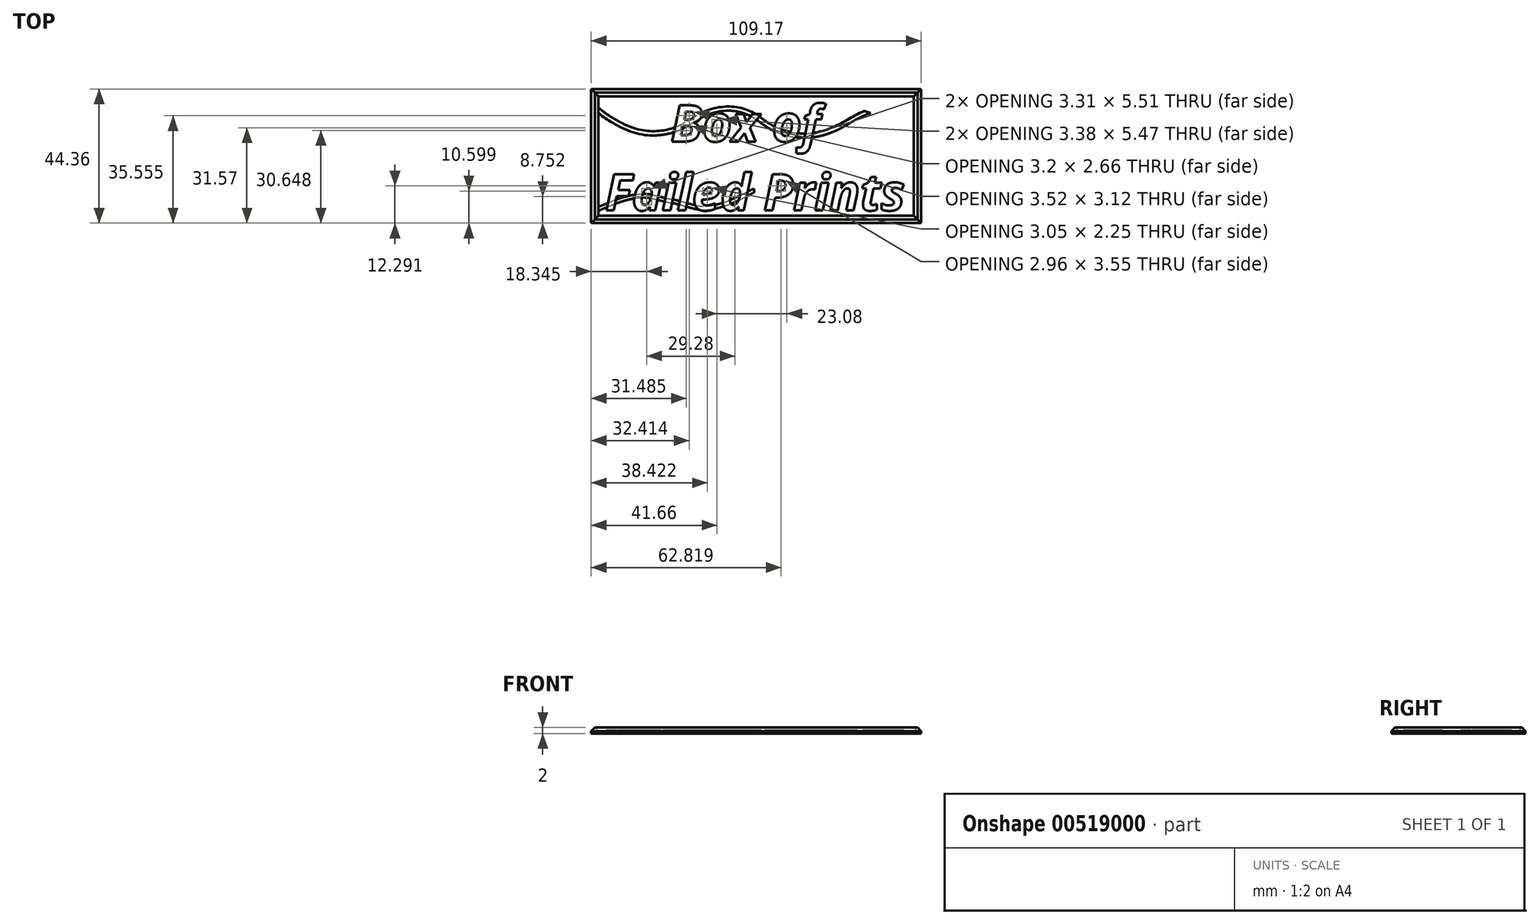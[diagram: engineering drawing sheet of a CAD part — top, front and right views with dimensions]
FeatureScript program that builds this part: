
annotation { "Feature Type Name" : "Feature", "Feature Type Description" : "" }
export const myFeature = defineFeature(function(context is Context, id is Id, definition is map)
    precondition{}
    {
        {
            var Q0;
            Q0=qCreatedBy(makeId("Top.planeOp"),FACE);
            var sketch = newSketch(context, id + "F0", { "sketchPlane" : qUnion([Q0])});
            skText(sketch, "E0", { "text": "     Box of\nFailed Prints", "fontName": "OpenSans-BoldItalic.ttf"});
            skPoint(sketch, "E1", {"position": v(22.9, -6.3) * mm});
            skPoint(sketch, "E2", {"position": v(16.26, 3.29) * mm});
            skPoint(sketch, "E3", {"position": v(-27.04, 4.89) * mm});
            skPoint(sketch, "E4", {"position": v(-27.69, -6.3) * mm});
            skPoint(sketch, "E5", {"position": v(-42.06, -6.3) * mm});
            skPoint(sketch, "E6", {"position": v(38.07, -7.94) * mm});
            skPoint(sketch, "E7", {"position": v(3.67, -16.5) * mm});
            skPoint(sketch, "E8", {"position": v(-5.3, -16.52) * mm});
            skPoint(sketch, "E9", {"position": v(-5.3, 13.1) * mm});
            const initialGuessF0  = {"E0": [-0.0504, 0.00489, 1, 0, 0.01208]};
            skSetInitialGuess(sketch, initialGuessF0);
            skSolve(sketch);
        }
        {
            var Q0;
            Q0=qCreatedBy(makeId("Top.planeOp"),FACE);
            var sketch = newSketch(context, id + "F1", { "sketchPlane" : qUnion([Q0])});
            skLineSegment(sketch, "E10.bottom", {"start": v(-53.75, 21.06) * mm, "end": v(53.02, 21.06) * mm});
            skLineSegment(sketch, "E10.top", {"start": v(-53.75, -20.9) * mm, "end": v(53.02, -20.9) * mm});
            skLineSegment(sketch, "E10.left", {"start": v(-53.75, 21.06) * mm, "end": v(-53.75, -20.9) * mm});
            skLineSegment(sketch, "E10.right", {"start": v(53.02, 21.06) * mm, "end": v(53.02, -20.9) * mm});
            skLineSegment(sketch, "E11.1", {"start": v(-52.57, 19.86) * mm, "end": v(51.82, 19.86) * mm});
            skLineSegment(sketch, "E11.3", {"start": v(-52.55, -19.72) * mm, "end": v(51.83, -19.66) * mm});
            skPoint(sketch, "E12.3", {"position": v(-5.3, -16.52) * mm});
            skPoint(sketch, "E12.4", {"position": v(-27.69, -6.3) * mm});
            skPoint(sketch, "E12.5", {"position": v(-42.06, -6.3) * mm});
            skPoint(sketch, "E12.6", {"position": v(3.67, -16.5) * mm});
            skPoint(sketch, "E12.7", {"position": v(22.9, -6.3) * mm});
            skPoint(sketch, "E12.8", {"position": v(38.07, -7.94) * mm});
            skPoint(sketch, "E13.3.internal.snap0", {"position": v(-0.45, -13.25) * mm});
            skLineSegment(sketch, "E14.0", {"start": v(-54.95, 22.26) * mm, "end": v(54.22, 22.26) * mm});
            skLineSegment(sketch, "E14.1", {"start": v(-54.95, 22.26) * mm, "end": v(-54.95, -22.1) * mm});
            skLineSegment(sketch, "E14.2", {"start": v(-54.95, -22.1) * mm, "end": v(54.22, -22.1) * mm});
            skLineSegment(sketch, "E14.3", {"start": v(54.22, 22.26) * mm, "end": v(54.22, -22.1) * mm});
            skFitSpline(sketch, "E15", {"points": [v(-52.55, -16.74) * mm, v(-45.87, -14.06) * mm, v(-37.44, -12.43) * mm, v(-31.84, -13.48) * mm, v(-24.84, -15) * mm, v(-18.3, -16.51) * mm, v(-9.66, -14.76) * mm, v(-1.84, -11.02) * mm, v(3.76, -8.8) * mm, v(9.6, -8.37) * mm, v(13.33, -9.5) * mm, v(17.65, -13.24) * mm, v(26.29, -14.64) * mm, v(35.04, -13.48) * mm, v(43.68, -9.97) * mm, v(51.82, -6.94) * mm], "startDerivative": vector(94.52, 42) * mm, "endDerivative": vector(110.86, 38.48) * mm});
            skFitSpline(sketch, "E16.0", {"points": [v(-52.07, -17.84) * mm, v(-51.08, -17.4) * mm, v(-49.62, -16.75) * mm, v(-47.57, -15.93) * mm, v(-45.95, -15.34) * mm, v(-44.2, -14.78) * mm, v(-42.4, -14.29) * mm, v(-40.58, -13.9) * mm, v(-39.13, -13.7) * mm, v(-38.06, -13.63) * mm, v(-37.31, -13.62) * mm, v(-36.6, -13.66) * mm, v(-35.7, -13.78) * mm, v(-34.59, -14) * mm, v(-33.42, -14.31) * mm, v(-32.42, -14.57) * mm, v(-31.36, -14.82) * mm, v(-30, -15.1) * mm, v(-28.3, -15.43) * mm, v(-26.92, -15.72) * mm, v(-25.83, -15.97) * mm, v(-25.05, -16.18) * mm, v(-24.27, -16.4) * mm, v(-23.23, -16.7) * mm, v(-21.92, -17.1) * mm, v(-20.54, -17.44) * mm, v(-19.37, -17.63) * mm, v(-18.45, -17.72) * mm, v(-17.5, -17.74) * mm, v(-16.23, -17.68) * mm, v(-14.6, -17.46) * mm, v(-12.63, -17.02) * mm, v(-10.67, -16.42) * mm, v(-8.11, -15.47) * mm, v(-5.71, -14.35) * mm, v(-3.49, -13.22) * mm, v(-1.92, -12.4) * mm, v(-0.45, -11.66) * mm, v(0.92, -11.02) * mm, v(2.25, -10.48) * mm, v(3.36, -10.13) * mm, v(4.28, -9.92) * mm, v(5.24, -9.74) * mm, v(6.47, -9.59) * mm, v(7.7, -9.53) * mm, v(8.64, -9.53) * mm, v(9.32, -9.55) * mm, v(9.96, -9.6) * mm, v(10.73, -9.7) * mm, v(11.4, -9.85) * mm, v(11.98, -10.09) * mm, v(12.4, -10.31) * mm, v(12.8, -10.6) * mm, v(13.24, -10.99) * mm, v(13.72, -11.46) * mm, v(14.41, -12.16) * mm, v(15.2, -12.95) * mm, v(16.13, -13.7) * mm, v(16.79, -14.14) * mm, v(17.36, -14.45) * mm, v(17.95, -14.73) * mm, v(18.71, -15.03) * mm, v(19.67, -15.3) * mm, v(20.99, -15.58) * mm, v(22.69, -15.78) * mm, v(24.41, -15.85) * mm, v(25.77, -15.85) * mm, v(27.1, -15.83) * mm, v(28.74, -15.76) * mm, v(30.67, -15.6) * mm, v(32.58, -15.31) * mm, v(34.47, -14.9) * mm, v(36.36, -14.34) * mm, v(38.21, -13.65) * mm, v(40.04, -12.89) * mm, v(41.83, -12.1) * mm, v(43.59, -11.31) * mm, v(45.31, -10.59) * mm, v(47.04, -9.92) * mm, v(49.34, -9.07) * mm, v(51.06, -8.47) * mm, v(52.22, -8.07) * mm]});
            skFitSpline(sketch, "E17", {"points": [v(-45.87, -14.06) * mm, v(-42.3, -9.7) * mm, v(-42.06, -6.3) * mm, v(-43.55, -3.6) * mm, v(-47.16, -3.05) * mm], "startDerivative": vector(14.66, 14.42) * mm, "endDerivative": vector(-16.79, -0.25) * mm});
            skFitSpline(sketch, "E18", {"points": [v(-43.62, -13.38) * mm, v(-41.38, -9.83) * mm, v(-41.09, -6.74) * mm, v(-42.06, -4.11) * mm, v(-43.2, -2.89) * mm, v(-45.87, -2.24) * mm, v(-47.16, -3.05) * mm], "startDerivative": vector(12.11, 17.54) * mm, "endDerivative": vector(-8.35, -8.39) * mm});
            skFitSpline(sketch, "E19", {"points": [v(-41.3, -14.06) * mm, v(-38.04, -16.51) * mm, v(-31.84, -17.56) * mm, v(-27.98, -17.21) * mm], "startDerivative": vector(8.92, -8.87) * mm, "endDerivative": vector(11.58, 1.72) * mm});
            skFitSpline(sketch, "E20", {"points": [v(-42.64, -14.37) * mm, v(-39.3, -17.28) * mm, v(-33.53, -18.39) * mm, v(-29.44, -18.04) * mm, v(-27.98, -17.21) * mm], "startDerivative": vector(10.87, -12.4) * mm, "endDerivative": vector(7.58, 5.67) * mm});
            skFitSpline(sketch, "E21", {"points": [v(-33.72, -13) * mm, v(-30.55, -11.87) * mm, v(-27.15, -10.06) * mm, v(-26.04, -8.19) * mm, v(-26.45, -7.15) * mm, v(-27.69, -6.3) * mm, v(-30.62, -6.3) * mm, v(-31.84, -7.08) * mm], "startDerivative": vector(17.57, 6.72) * mm, "endDerivative": vector(-8.56, -7.92) * mm});
            skFitSpline(sketch, "E22", {"points": [v(-31.84, -13.48) * mm, v(-27.69, -11.73) * mm, v(-25.55, -9.58) * mm, v(-25.06, -7.91) * mm, v(-25.83, -6.76) * mm, v(-27.07, -5.92) * mm, v(-28.5, -5.75) * mm, v(-30.22, -5.88) * mm, v(-31.3, -6.3) * mm, v(-31.84, -7.08) * mm], "startDerivative": vector(25.72, 8.64) * mm, "endDerivative": vector(-5.63, -10.85) * mm});
            skFitSpline(sketch, "E23", {"points": [v(-22.57, -15.65) * mm, v(-19.68, -14.06) * mm, v(-18.3, -10.78) * mm, v(-17.12, -8.19) * mm, v(-14.31, -7.08) * mm, v(-12.74, -6.3) * mm, v(-11.92, -4.5) * mm, v(-12.41, -3.05) * mm], "startDerivative": vector(19.95, 7.04) * mm, "endDerivative": vector(-6.86, 12.25) * mm});
            skFitSpline(sketch, "E24", {"points": [v(-20.8, -16.14) * mm, v(-19.27, -15) * mm, v(-17.61, -12.61) * mm, v(-16.87, -9.37) * mm, v(-15.4, -8.19) * mm, v(-12.74, -7.08) * mm, v(-11.52, -5.03) * mm, v(-11.66, -3.7) * mm, v(-12.41, -3.05) * mm], "startDerivative": vector(13, 5.53) * mm, "endDerivative": vector(-10.05, 6.42) * mm});
            skFitSpline(sketch, "E25", {"points": [v(-6.4, -14.66) * mm, v(-2.78, -15.38) * mm, v(-0.67, -14.06) * mm, v(-0.45, -13.25) * mm, v(-0.45, -10.34) * mm, v(-1.11, -8.66) * mm, v(-2.53, -7.08) * mm, v(-4.97, -6.3) * mm, v(-6.6, -6.3) * mm, v(-7.74, -5.66) * mm, v(-7.84, -4.2) * mm], "startDerivative": vector(27.63, -11.22) * mm, "endDerivative": vector(2.22, 19.13) * mm});
            skFitSpline(sketch, "E26", {"points": [v(-4.97, -14.06) * mm, v(-3.47, -14.66) * mm, v(-1.9, -14.06) * mm, v(-1.26, -13.25) * mm, v(-1.06, -11.21) * mm, v(-1.55, -9.3) * mm, v(-3.07, -7.58) * mm, v(-5.3, -7.08) * mm, v(-7.2, -6.77) * mm, v(-8.42, -5.66) * mm, v(-8.47, -4.74) * mm, v(-7.84, -4.2) * mm], "startDerivative": vector(15.88, -9.92) * mm, "endDerivative": vector(11.77, 7.08) * mm});
            skFitSpline(sketch, "E27", {"points": [v(8.18, -9.53) * mm, v(10.24, -12.97) * mm, v(14.53, -15) * mm, v(17.8, -14.66) * mm, v(21.88, -12.97) * mm, v(23.9, -9.5) * mm, v(23.9, -8.19) * mm, v(22.9, -6.3) * mm, v(20.64, -4.74) * mm, v(18.17, -4.74) * mm, v(18.25, -4.74) * mm], "startDerivative": vector(12.47, -29.94) * mm, "endDerivative": vector(7.3, 0.3) * mm});
            skFitSpline(sketch, "E28", {"points": [v(6.77, -9.58) * mm, v(8.84, -13.48) * mm, v(13.33, -15.68) * mm, v(17.34, -15.77) * mm, v(22.38, -13.48) * mm, v(24.54, -9.53) * mm, v(24.34, -7.68) * mm, v(22.9, -5.38) * mm, v(20.71, -4.2) * mm, v(18.25, -4.74) * mm], "startDerivative": vector(12.1, -34.35) * mm, "endDerivative": vector(-26.7, -10.01) * mm});
            skFitSpline(sketch, "E29", {"points": [v(32.32, -14.12) * mm, v(34.85, -12.79) * mm, v(37.2, -10.43) * mm, v(37.5, -8.12) * mm, v(36.37, -6.21) * mm, v(36.71, -4.5) * mm, v(38.13, -3.27) * mm, v(40.83, -3.36) * mm], "startDerivative": vector(16.32, 7.02) * mm, "endDerivative": vector(19.35, -3.3) * mm});
            skFitSpline(sketch, "E30", {"points": [v(36.21, -13.1) * mm, v(38.09, -10.82) * mm, v(38.43, -8.71) * mm, v(38.07, -7.94) * mm, v(36.88, -5.99) * mm, v(37.47, -4.37) * mm, v(38.67, -3.56) * mm, v(40.83, -3.36) * mm], "startDerivative": vector(12.78, 11.25) * mm, "endDerivative": vector(13.8, 2.6) * mm});
            skFitSpline(sketch, "E31.trimOffspring", {"points": [v(-52.07, -17.84) * mm, v(-51.08, -17.4) * mm, v(-49.62, -16.75) * mm, v(-47.57, -15.93) * mm, v(-45.95, -15.34) * mm, v(-44.2, -14.78) * mm, v(-42.4, -14.29) * mm, v(-40.58, -13.9) * mm, v(-39.13, -13.7) * mm, v(-38.06, -13.63) * mm, v(-37.31, -13.62) * mm, v(-36.6, -13.66) * mm, v(-35.7, -13.78) * mm, v(-34.59, -14) * mm, v(-33.42, -14.31) * mm, v(-32.42, -14.57) * mm, v(-31.36, -14.82) * mm, v(-30, -15.1) * mm, v(-28.3, -15.43) * mm, v(-26.92, -15.72) * mm, v(-25.83, -15.97) * mm, v(-25.05, -16.18) * mm, v(-24.27, -16.4) * mm, v(-23.23, -16.7) * mm, v(-21.92, -17.1) * mm, v(-20.54, -17.44) * mm, v(-19.37, -17.63) * mm, v(-18.45, -17.72) * mm, v(-17.5, -17.74) * mm, v(-16.23, -17.68) * mm, v(-14.6, -17.46) * mm, v(-12.63, -17.02) * mm, v(-10.67, -16.42) * mm, v(-8.11, -15.47) * mm, v(-5.71, -14.35) * mm, v(-3.49, -13.22) * mm, v(-1.92, -12.4) * mm, v(-0.45, -11.66) * mm, v(0.92, -11.02) * mm, v(2.25, -10.48) * mm, v(3.36, -10.13) * mm, v(4.28, -9.92) * mm, v(5.24, -9.74) * mm, v(6.47, -9.59) * mm, v(7.7, -9.53) * mm, v(8.64, -9.53) * mm, v(9.32, -9.55) * mm, v(9.96, -9.6) * mm, v(10.73, -9.7) * mm, v(11.4, -9.85) * mm, v(11.98, -10.09) * mm, v(12.4, -10.31) * mm, v(12.8, -10.6) * mm, v(13.24, -10.99) * mm, v(13.72, -11.46) * mm, v(14.41, -12.16) * mm, v(15.2, -12.95) * mm, v(16.13, -13.7) * mm, v(16.79, -14.14) * mm, v(17.36, -14.45) * mm, v(17.95, -14.73) * mm, v(18.71, -15.03) * mm, v(19.67, -15.3) * mm, v(20.99, -15.58) * mm, v(22.69, -15.78) * mm, v(24.41, -15.85) * mm, v(25.77, -15.85) * mm, v(27.1, -15.83) * mm, v(28.74, -15.76) * mm, v(30.67, -15.6) * mm, v(32.58, -15.31) * mm, v(34.47, -14.9) * mm, v(36.36, -14.34) * mm, v(38.21, -13.65) * mm, v(40.04, -12.89) * mm, v(41.83, -12.1) * mm, v(43.59, -11.31) * mm, v(45.31, -10.59) * mm, v(47.04, -9.92) * mm, v(49.34, -9.07) * mm, v(51.06, -8.47) * mm, v(52.22, -8.07) * mm]});
            skLineSegment(sketch, "E32", {"start": v(-52.07, -17.84) * mm, "end": v(-52.55, -17.84) * mm});
            skLineSegment(sketch, "E33", {"start": v(-52.55, -17.84) * mm, "end": v(-52.07, -17.84) * mm});
            skFitSpline(sketch, "E34.trimOffspring", {"points": [v(-52.07, -17.84) * mm, v(-51.08, -17.4) * mm, v(-49.62, -16.75) * mm, v(-47.57, -15.93) * mm, v(-45.95, -15.34) * mm, v(-44.2, -14.78) * mm, v(-42.4, -14.29) * mm, v(-40.58, -13.9) * mm, v(-39.13, -13.7) * mm, v(-38.06, -13.63) * mm, v(-37.31, -13.62) * mm, v(-36.6, -13.66) * mm, v(-35.7, -13.78) * mm, v(-34.59, -14) * mm, v(-33.42, -14.31) * mm, v(-32.42, -14.57) * mm, v(-31.36, -14.82) * mm, v(-30, -15.1) * mm, v(-28.3, -15.43) * mm, v(-26.92, -15.72) * mm, v(-25.83, -15.97) * mm, v(-25.05, -16.18) * mm, v(-24.27, -16.4) * mm, v(-23.23, -16.7) * mm, v(-21.92, -17.1) * mm, v(-20.54, -17.44) * mm, v(-19.37, -17.63) * mm, v(-18.45, -17.72) * mm, v(-17.5, -17.74) * mm, v(-16.23, -17.68) * mm, v(-14.6, -17.46) * mm, v(-12.63, -17.02) * mm, v(-10.67, -16.42) * mm, v(-8.11, -15.47) * mm, v(-5.71, -14.35) * mm, v(-3.49, -13.22) * mm, v(-1.92, -12.4) * mm, v(-0.45, -11.66) * mm, v(0.92, -11.02) * mm, v(2.25, -10.48) * mm, v(3.36, -10.13) * mm, v(4.28, -9.92) * mm, v(5.24, -9.74) * mm, v(6.47, -9.59) * mm, v(7.7, -9.53) * mm, v(8.64, -9.53) * mm, v(9.32, -9.55) * mm, v(9.96, -9.6) * mm, v(10.73, -9.7) * mm, v(11.4, -9.85) * mm, v(11.98, -10.09) * mm, v(12.4, -10.31) * mm, v(12.8, -10.6) * mm, v(13.24, -10.99) * mm, v(13.72, -11.46) * mm, v(14.41, -12.16) * mm, v(15.2, -12.95) * mm, v(16.13, -13.7) * mm, v(16.79, -14.14) * mm, v(17.36, -14.45) * mm, v(17.95, -14.73) * mm, v(18.71, -15.03) * mm, v(19.67, -15.3) * mm, v(20.99, -15.58) * mm, v(22.69, -15.78) * mm, v(24.41, -15.85) * mm, v(25.77, -15.85) * mm, v(27.1, -15.83) * mm, v(28.74, -15.76) * mm, v(30.67, -15.6) * mm, v(32.58, -15.31) * mm, v(34.47, -14.9) * mm, v(36.36, -14.34) * mm, v(38.21, -13.65) * mm, v(40.04, -12.89) * mm, v(41.83, -12.1) * mm, v(43.59, -11.31) * mm, v(45.31, -10.59) * mm, v(47.04, -9.92) * mm, v(49.34, -9.07) * mm, v(51.06, -8.47) * mm, v(52.22, -8.07) * mm]});
            skFitSpline(sketch, "E35.trimOffspring", {"points": [v(-52.07, -17.84) * mm, v(-51.08, -17.4) * mm, v(-49.62, -16.75) * mm, v(-47.57, -15.93) * mm, v(-45.95, -15.34) * mm, v(-44.2, -14.78) * mm, v(-42.4, -14.29) * mm, v(-40.58, -13.9) * mm, v(-39.13, -13.7) * mm, v(-38.06, -13.63) * mm, v(-37.31, -13.62) * mm, v(-36.6, -13.66) * mm, v(-35.7, -13.78) * mm, v(-34.59, -14) * mm, v(-33.42, -14.31) * mm, v(-32.42, -14.57) * mm, v(-31.36, -14.82) * mm, v(-30, -15.1) * mm, v(-28.3, -15.43) * mm, v(-26.92, -15.72) * mm, v(-25.83, -15.97) * mm, v(-25.05, -16.18) * mm, v(-24.27, -16.4) * mm, v(-23.23, -16.7) * mm, v(-21.92, -17.1) * mm, v(-20.54, -17.44) * mm, v(-19.37, -17.63) * mm, v(-18.45, -17.72) * mm, v(-17.5, -17.74) * mm, v(-16.23, -17.68) * mm, v(-14.6, -17.46) * mm, v(-12.63, -17.02) * mm, v(-10.67, -16.42) * mm, v(-8.11, -15.47) * mm, v(-5.71, -14.35) * mm, v(-3.49, -13.22) * mm, v(-1.92, -12.4) * mm, v(-0.45, -11.66) * mm, v(0.92, -11.02) * mm, v(2.25, -10.48) * mm, v(3.36, -10.13) * mm, v(4.28, -9.92) * mm, v(5.24, -9.74) * mm, v(6.47, -9.59) * mm, v(7.7, -9.53) * mm, v(8.64, -9.53) * mm, v(9.32, -9.55) * mm, v(9.96, -9.6) * mm, v(10.73, -9.7) * mm, v(11.4, -9.85) * mm, v(11.98, -10.09) * mm, v(12.4, -10.31) * mm, v(12.8, -10.6) * mm, v(13.24, -10.99) * mm, v(13.72, -11.46) * mm, v(14.41, -12.16) * mm, v(15.2, -12.95) * mm, v(16.13, -13.7) * mm, v(16.79, -14.14) * mm, v(17.36, -14.45) * mm, v(17.95, -14.73) * mm, v(18.71, -15.03) * mm, v(19.67, -15.3) * mm, v(20.99, -15.58) * mm, v(22.69, -15.78) * mm, v(24.41, -15.85) * mm, v(25.77, -15.85) * mm, v(27.1, -15.83) * mm, v(28.74, -15.76) * mm, v(30.67, -15.6) * mm, v(32.58, -15.31) * mm, v(34.47, -14.9) * mm, v(36.36, -14.34) * mm, v(38.21, -13.65) * mm, v(40.04, -12.89) * mm, v(41.83, -12.1) * mm, v(43.59, -11.31) * mm, v(45.31, -10.59) * mm, v(47.04, -9.92) * mm, v(49.34, -9.07) * mm, v(51.06, -8.47) * mm, v(52.22, -8.07) * mm]});
            skLineSegment(sketch, "E36", {"start": v(-4.97, -14.06) * mm, "end": v(-5.07, -14.02) * mm});
            skFitSpline(sketch, "E37.trimOffspring", {"points": [v(-52.07, -17.84) * mm, v(-51.08, -17.4) * mm, v(-49.62, -16.75) * mm, v(-47.57, -15.93) * mm, v(-45.95, -15.34) * mm, v(-44.2, -14.78) * mm, v(-42.4, -14.29) * mm, v(-40.58, -13.9) * mm, v(-39.13, -13.7) * mm, v(-38.06, -13.63) * mm, v(-37.31, -13.62) * mm, v(-36.6, -13.66) * mm, v(-35.7, -13.78) * mm, v(-34.59, -14) * mm, v(-33.42, -14.31) * mm, v(-32.42, -14.57) * mm, v(-31.36, -14.82) * mm, v(-30, -15.1) * mm, v(-28.3, -15.43) * mm, v(-26.92, -15.72) * mm, v(-25.83, -15.97) * mm, v(-25.05, -16.18) * mm, v(-24.27, -16.4) * mm, v(-23.23, -16.7) * mm, v(-21.92, -17.1) * mm, v(-20.54, -17.44) * mm, v(-19.37, -17.63) * mm, v(-18.45, -17.72) * mm, v(-17.5, -17.74) * mm, v(-16.23, -17.68) * mm, v(-14.6, -17.46) * mm, v(-12.63, -17.02) * mm, v(-10.67, -16.42) * mm, v(-8.11, -15.47) * mm, v(-5.71, -14.35) * mm, v(-3.49, -13.22) * mm, v(-1.92, -12.4) * mm, v(-0.45, -11.66) * mm, v(0.92, -11.02) * mm, v(2.25, -10.48) * mm, v(3.36, -10.13) * mm, v(4.28, -9.92) * mm, v(5.24, -9.74) * mm, v(6.47, -9.59) * mm, v(7.7, -9.53) * mm, v(8.64, -9.53) * mm, v(9.32, -9.55) * mm, v(9.96, -9.6) * mm, v(10.73, -9.7) * mm, v(11.4, -9.85) * mm, v(11.98, -10.09) * mm, v(12.4, -10.31) * mm, v(12.8, -10.6) * mm, v(13.24, -10.99) * mm, v(13.72, -11.46) * mm, v(14.41, -12.16) * mm, v(15.2, -12.95) * mm, v(16.13, -13.7) * mm, v(16.79, -14.14) * mm, v(17.36, -14.45) * mm, v(17.95, -14.73) * mm, v(18.71, -15.03) * mm, v(19.67, -15.3) * mm, v(20.99, -15.58) * mm, v(22.69, -15.78) * mm, v(24.41, -15.85) * mm, v(25.77, -15.85) * mm, v(27.1, -15.83) * mm, v(28.74, -15.76) * mm, v(30.67, -15.6) * mm, v(32.58, -15.31) * mm, v(34.47, -14.9) * mm, v(36.36, -14.34) * mm, v(38.21, -13.65) * mm, v(40.04, -12.89) * mm, v(41.83, -12.1) * mm, v(43.59, -11.31) * mm, v(45.31, -10.59) * mm, v(47.04, -9.92) * mm, v(49.34, -9.07) * mm, v(51.06, -8.47) * mm, v(52.22, -8.07) * mm]});
            skFitSpline(sketch, "E38.trimOffspring", {"points": [v(-52.07, -17.84) * mm, v(-51.08, -17.4) * mm, v(-49.62, -16.75) * mm, v(-47.57, -15.93) * mm, v(-45.95, -15.34) * mm, v(-44.2, -14.78) * mm, v(-42.4, -14.29) * mm, v(-40.58, -13.9) * mm, v(-39.13, -13.7) * mm, v(-38.06, -13.63) * mm, v(-37.31, -13.62) * mm, v(-36.6, -13.66) * mm, v(-35.7, -13.78) * mm, v(-34.59, -14) * mm, v(-33.42, -14.31) * mm, v(-32.42, -14.57) * mm, v(-31.36, -14.82) * mm, v(-30, -15.1) * mm, v(-28.3, -15.43) * mm, v(-26.92, -15.72) * mm, v(-25.83, -15.97) * mm, v(-25.05, -16.18) * mm, v(-24.27, -16.4) * mm, v(-23.23, -16.7) * mm, v(-21.92, -17.1) * mm, v(-20.54, -17.44) * mm, v(-19.37, -17.63) * mm, v(-18.45, -17.72) * mm, v(-17.5, -17.74) * mm, v(-16.23, -17.68) * mm, v(-14.6, -17.46) * mm, v(-12.63, -17.02) * mm, v(-10.67, -16.42) * mm, v(-8.11, -15.47) * mm, v(-5.71, -14.35) * mm, v(-3.49, -13.22) * mm, v(-1.92, -12.4) * mm, v(-0.45, -11.66) * mm, v(0.92, -11.02) * mm, v(2.25, -10.48) * mm, v(3.36, -10.13) * mm, v(4.28, -9.92) * mm, v(5.24, -9.74) * mm, v(6.47, -9.59) * mm, v(7.7, -9.53) * mm, v(8.64, -9.53) * mm, v(9.32, -9.55) * mm, v(9.96, -9.6) * mm, v(10.73, -9.7) * mm, v(11.4, -9.85) * mm, v(11.98, -10.09) * mm, v(12.4, -10.31) * mm, v(12.8, -10.6) * mm, v(13.24, -10.99) * mm, v(13.72, -11.46) * mm, v(14.41, -12.16) * mm, v(15.2, -12.95) * mm, v(16.13, -13.7) * mm, v(16.79, -14.14) * mm, v(17.36, -14.45) * mm, v(17.95, -14.73) * mm, v(18.71, -15.03) * mm, v(19.67, -15.3) * mm, v(20.99, -15.58) * mm, v(22.69, -15.78) * mm, v(24.41, -15.85) * mm, v(25.77, -15.85) * mm, v(27.1, -15.83) * mm, v(28.74, -15.76) * mm, v(30.67, -15.6) * mm, v(32.58, -15.31) * mm, v(34.47, -14.9) * mm, v(36.36, -14.34) * mm, v(38.21, -13.65) * mm, v(40.04, -12.89) * mm, v(41.83, -12.1) * mm, v(43.59, -11.31) * mm, v(45.31, -10.59) * mm, v(47.04, -9.92) * mm, v(49.34, -9.07) * mm, v(51.06, -8.47) * mm, v(52.22, -8.07) * mm]});
            skPoint(sketch, "E39.end.orphan", {"position": v(5.4, -8.37) * mm});
            skLineSegment(sketch, "E40.trimOffspring", {"start": v(51.82, -8.2) * mm, "end": v(51.83, -19.66) * mm});
            skLineSegment(sketch, "E41", {"start": v(-52.57, 19.86) * mm, "end": v(-52.55, -19.72) * mm});
            skLineSegment(sketch, "E42", {"start": v(-52.57, 19.86) * mm, "end": v(-54.95, 22.26) * mm});
            skLineSegment(sketch, "E43", {"start": v(-52.55, -19.72) * mm, "end": v(-54.95, -22.1) * mm});
            skLineSegment(sketch, "E44", {"start": v(-52.55, -16.74) * mm, "end": v(-47.44, -14.6) * mm});
            skLineSegment(sketch, "E45.trimOffspring", {"start": v(51.82, -6.94) * mm, "end": v(51.83, -19.66) * mm});
            skLineSegment(sketch, "E46", {"start": v(51.82, 19.86) * mm, "end": v(51.82, -6.94) * mm});
            skFitSpline(sketch, "E47", {"points": [v(-52.57, 16.08) * mm, v(-49.1, 13.5) * mm, v(-40.35, 9.2) * mm, v(-31.83, 8.5) * mm, v(-25.06, 10.6) * mm, v(-17, 15.03) * mm, v(-6.97, 16.31) * mm, v(0, 13.63) * mm, v(4.82, 10.36) * mm, v(14.4, 7.56) * mm, v(25.13, 9.66) * mm, v(33.42, 14.1) * mm, v(43, 16.66) * mm, v(50.11, 14.91) * mm, v(51.82, 13.5) * mm], "startDerivative": vector(55.97, -44.86) * mm, "endDerivative": vector(34.72, -36.64) * mm});
            skFitSpline(sketch, "E48.0", {"points": [v(-53.44, 14.99) * mm, v(-53.15, 14.75) * mm, v(-52.56, 14.28) * mm, v(-51.58, 13.52) * mm, v(-50.63, 12.85) * mm, v(-49.76, 12.26) * mm, v(-48.8, 11.65) * mm, v(-47.47, 10.85) * mm, v(-45.7, 9.88) * mm, v(-43.8, 8.97) * mm, v(-41.82, 8.17) * mm, v(-39.81, 7.55) * mm, v(-37.84, 7.15) * mm, v(-35.9, 6.94) * mm, v(-34.03, 6.9) * mm, v(-32.22, 7.02) * mm, v(-30.48, 7.25) * mm, v(-28.8, 7.62) * mm, v(-27.15, 8.13) * mm, v(-25.8, 8.67) * mm, v(-24.72, 9.18) * mm, v(-23.65, 9.75) * mm, v(-22.35, 10.52) * mm, v(-20.79, 11.48) * mm, v(-19.21, 12.41) * mm, v(-17.6, 13.27) * mm, v(-15.94, 13.97) * mm, v(-14.16, 14.51) * mm, v(-12.32, 14.89) * mm, v(-10.48, 15.08) * mm, v(-8.97, 15.1) * mm, v(-7.81, 15.01) * mm, v(-6.7, 14.87) * mm, v(-5.35, 14.57) * mm, v(-3.85, 14.07) * mm, v(-2.45, 13.44) * mm, v(-1.17, 12.73) * mm, v(-0.02, 11.97) * mm, v(1.09, 11.16) * mm, v(2.27, 10.3) * mm, v(3.61, 9.41) * mm, v(5.2, 8.55) * mm, v(6.98, 7.77) * mm, v(8.94, 7.1) * mm, v(11.02, 6.57) * mm, v(13.2, 6.21) * mm, v(15.42, 6.09) * mm, v(17.63, 6.2) * mm, v(19.8, 6.51) * mm, v(21.9, 7) * mm, v(23.93, 7.64) * mm, v(25.85, 8.42) * mm, v(27.63, 9.29) * mm, v(29.3, 10.2) * mm, v(30.9, 11.13) * mm, v(32.5, 12.04) * mm, v(34.1, 12.89) * mm, v(35.77, 13.66) * mm, v(37.5, 14.31) * mm, v(39.27, 14.83) * mm, v(40.74, 15.11) * mm, v(41.9, 15.23) * mm, v(42.77, 15.27) * mm, v(43.63, 15.25) * mm, v(44.78, 15.15) * mm, v(46.18, 14.9) * mm, v(47.44, 14.54) * mm, v(48.32, 14.22) * mm, v(48.9, 13.97) * mm, v(49.38, 13.72) * mm, v(49.75, 13.5) * mm, v(50.05, 13.27) * mm, v(50.39, 12.98) * mm, v(50.62, 12.74) * mm, v(50.8, 12.55) * mm]});
            skLineSegment(sketch, "E49", {"start": v(50.8, 12.55) * mm, "end": v(51.82, 11.45) * mm});
            skFitSpline(sketch, "E50", {"points": [v(-46.15, 11.73) * mm, v(-38.67, 12.15) * mm, v(-36.08, 14.24) * mm, v(-36.94, 15.97) * mm, v(-39.65, 16.46) * mm, v(-40.51, 15.35) * mm], "startDerivative": vector(26.26, -1.25) * mm, "endDerivative": vector(-4.24, -10.15) * mm});
            skFitSpline(sketch, "E51", {"points": [v(-44.2, 10.72) * mm, v(-39.99, 10.87) * mm, v(-36.44, 12.33) * mm, v(-35.34, 14.3) * mm, v(-35.78, 15.63) * mm, v(-36.92, 16.54) * mm, v(-38.49, 17.02) * mm, v(-39.88, 16.94) * mm, v(-40.46, 16.21) * mm, v(-40.51, 15.35) * mm], "startDerivative": vector(25.11, -0.87) * mm, "endDerivative": vector(0.73, -11.43) * mm});
            skFitSpline(sketch, "E52.trimOffspring", {"points": [v(-52.57, 16.08) * mm, v(-49.1, 13.5) * mm, v(-40.35, 9.2) * mm, v(-31.83, 8.5) * mm, v(-25.06, 10.6) * mm, v(-17, 15.03) * mm, v(-6.97, 16.31) * mm, v(0, 13.63) * mm, v(4.82, 10.36) * mm, v(14.4, 7.56) * mm, v(25.13, 9.66) * mm, v(33.42, 14.1) * mm, v(43, 16.66) * mm, v(50.11, 14.91) * mm, v(51.82, 13.5) * mm], "startDerivative": vector(55.97, -44.86) * mm, "endDerivative": vector(34.72, -36.64) * mm});
            skFitSpline(sketch, "E53", {"points": [v(-33.26, 6.96) * mm, v(-31.83, 5.05) * mm, v(-28.54, 3.22) * mm, v(-24.48, 3.52) * mm, v(-23.01, 4.8) * mm, v(-21.59, 6.11) * mm, v(-19.83, 6.33) * mm, v(-18.26, 5.57) * mm, v(-17.93, 5.05) * mm], "startDerivative": vector(9.14, -14.66) * mm, "endDerivative": vector(3.25, -7.53) * mm});
            skFitSpline(sketch, "E54", {"points": [v(-34.54, 6.93) * mm, v(-32.97, 5.2) * mm, v(-30.92, 3.52) * mm, v(-28.43, 2.53) * mm, v(-25.83, 2.57) * mm, v(-24.08, 3.11) * mm, v(-22.76, 4.52) * mm, v(-21.67, 5.66) * mm, v(-20.51, 6.15) * mm, v(-19.33, 5.94) * mm, v(-18.53, 5.57) * mm, v(-17.93, 5.05) * mm], "startDerivative": vector(14.25, -16.4) * mm, "endDerivative": vector(9.39, -8.93) * mm});
            skFitSpline(sketch, "E55.trimOffspring", {"points": [v(-53.44, 14.99) * mm, v(-53.15, 14.75) * mm, v(-52.56, 14.28) * mm, v(-51.58, 13.52) * mm, v(-50.63, 12.85) * mm, v(-49.76, 12.26) * mm, v(-48.8, 11.65) * mm, v(-47.47, 10.85) * mm, v(-45.7, 9.88) * mm, v(-43.8, 8.97) * mm, v(-41.82, 8.17) * mm, v(-39.81, 7.55) * mm, v(-37.84, 7.15) * mm, v(-35.9, 6.94) * mm, v(-34.03, 6.9) * mm, v(-32.22, 7.02) * mm, v(-30.48, 7.25) * mm, v(-28.8, 7.62) * mm, v(-27.15, 8.13) * mm, v(-25.8, 8.67) * mm, v(-24.72, 9.18) * mm, v(-23.65, 9.75) * mm, v(-22.35, 10.52) * mm, v(-20.79, 11.48) * mm, v(-19.21, 12.41) * mm, v(-17.6, 13.27) * mm, v(-15.94, 13.97) * mm, v(-14.16, 14.51) * mm, v(-12.32, 14.89) * mm, v(-10.48, 15.08) * mm, v(-8.97, 15.1) * mm, v(-7.81, 15.01) * mm, v(-6.7, 14.87) * mm, v(-5.35, 14.57) * mm, v(-3.85, 14.07) * mm, v(-2.45, 13.44) * mm, v(-1.17, 12.73) * mm, v(-0.02, 11.97) * mm, v(1.09, 11.16) * mm, v(2.27, 10.3) * mm, v(3.61, 9.41) * mm, v(5.2, 8.55) * mm, v(6.98, 7.77) * mm, v(8.94, 7.1) * mm, v(11.02, 6.57) * mm, v(13.2, 6.21) * mm, v(15.42, 6.09) * mm, v(17.63, 6.2) * mm, v(19.8, 6.51) * mm, v(21.9, 7) * mm, v(23.93, 7.64) * mm, v(25.85, 8.42) * mm, v(27.63, 9.29) * mm, v(29.3, 10.2) * mm, v(30.9, 11.13) * mm, v(32.5, 12.04) * mm, v(34.1, 12.89) * mm, v(35.77, 13.66) * mm, v(37.5, 14.31) * mm, v(39.27, 14.83) * mm, v(40.74, 15.11) * mm, v(41.9, 15.23) * mm, v(42.77, 15.27) * mm, v(43.63, 15.25) * mm, v(44.78, 15.15) * mm, v(46.18, 14.9) * mm, v(47.44, 14.54) * mm, v(48.32, 14.22) * mm, v(48.9, 13.97) * mm, v(49.38, 13.72) * mm, v(49.75, 13.5) * mm, v(50.05, 13.27) * mm, v(50.39, 12.98) * mm, v(50.62, 12.74) * mm, v(50.8, 12.55) * mm]});
            skFitSpline(sketch, "E56", {"points": [v(-19.85, 12.03) * mm, v(-16.5, 11.65) * mm, v(-11.84, 10.3) * mm, v(-8.94, 8.14) * mm, v(-7.29, 6.48) * mm, v(-5.12, 4.93) * mm, v(-1.5, 5.03) * mm, v(0, 6.48) * mm, v(1.1, 8.55) * mm, v(1.2, 8.45) * mm], "startDerivative": vector(24.63, -1.81) * mm, "endDerivative": vector(3.2, -6.58) * mm});
            skFitSpline(sketch, "E57", {"points": [v(-21.67, 10.94) * mm, v(-15.98, 10.2) * mm, v(-12.05, 9.2) * mm, v(-8.94, 6.69) * mm, v(-6.85, 4.93) * mm, v(-4.5, 4.1) * mm, v(-2.29, 4.15) * mm, v(-0.46, 4.84) * mm, v(0.8, 6.93) * mm, v(1.2, 8.45) * mm], "startDerivative": vector(37.95, -4.74) * mm, "endDerivative": vector(3.47, 17.32) * mm});
            skFitSpline(sketch, "E58.trimOffspring", {"points": [v(-53.44, 14.99) * mm, v(-53.15, 14.75) * mm, v(-52.56, 14.28) * mm, v(-51.58, 13.52) * mm, v(-50.63, 12.85) * mm, v(-49.76, 12.26) * mm, v(-48.8, 11.65) * mm, v(-47.47, 10.85) * mm, v(-45.7, 9.88) * mm, v(-43.8, 8.97) * mm, v(-41.82, 8.17) * mm, v(-39.81, 7.55) * mm, v(-37.84, 7.15) * mm, v(-35.9, 6.94) * mm, v(-34.03, 6.9) * mm, v(-32.22, 7.02) * mm, v(-30.48, 7.25) * mm, v(-28.8, 7.62) * mm, v(-27.15, 8.13) * mm, v(-25.8, 8.67) * mm, v(-24.72, 9.18) * mm, v(-23.65, 9.75) * mm, v(-22.35, 10.52) * mm, v(-20.79, 11.48) * mm, v(-19.21, 12.41) * mm, v(-17.6, 13.27) * mm, v(-15.94, 13.97) * mm, v(-14.16, 14.51) * mm, v(-12.32, 14.89) * mm, v(-10.48, 15.08) * mm, v(-8.97, 15.1) * mm, v(-7.81, 15.01) * mm, v(-6.7, 14.87) * mm, v(-5.35, 14.57) * mm, v(-3.85, 14.07) * mm, v(-2.45, 13.44) * mm, v(-1.17, 12.73) * mm, v(-0.02, 11.97) * mm, v(1.09, 11.16) * mm, v(2.27, 10.3) * mm, v(3.61, 9.41) * mm, v(5.2, 8.55) * mm, v(6.98, 7.77) * mm, v(8.94, 7.1) * mm, v(11.02, 6.57) * mm, v(13.2, 6.21) * mm, v(15.42, 6.09) * mm, v(17.63, 6.2) * mm, v(19.8, 6.51) * mm, v(21.9, 7) * mm, v(23.93, 7.64) * mm, v(25.85, 8.42) * mm, v(27.63, 9.29) * mm, v(29.3, 10.2) * mm, v(30.9, 11.13) * mm, v(32.5, 12.04) * mm, v(34.1, 12.89) * mm, v(35.77, 13.66) * mm, v(37.5, 14.31) * mm, v(39.27, 14.83) * mm, v(40.74, 15.11) * mm, v(41.9, 15.23) * mm, v(42.77, 15.27) * mm, v(43.63, 15.25) * mm, v(44.78, 15.15) * mm, v(46.18, 14.9) * mm, v(47.44, 14.54) * mm, v(48.32, 14.22) * mm, v(48.9, 13.97) * mm, v(49.38, 13.72) * mm, v(49.75, 13.5) * mm, v(50.05, 13.27) * mm, v(50.39, 12.98) * mm, v(50.62, 12.74) * mm, v(50.8, 12.55) * mm]});
            skFitSpline(sketch, "E59", {"points": [v(3.18, 11.39) * mm, v(5.55, 11.02) * mm, v(10.46, 10.94) * mm, v(14.07, 12.37) * mm, v(16.07, 14.68) * mm, v(18.34, 15.37) * mm, v(20.86, 14.8) * mm, v(22.6, 13.63) * mm, v(22.86, 12.41) * mm, v(22.38, 11.2) * mm], "startDerivative": vector(19.51, -3.65) * mm, "endDerivative": vector(-7.72, -14.98) * mm});
            skFitSpline(sketch, "E60", {"points": [v(4.82, 10.36) * mm, v(8.16, 10.02) * mm, v(11.64, 10.36) * mm, v(14.38, 11.8) * mm, v(15.9, 13.8) * mm, v(17.68, 14.76) * mm, v(20.16, 14.59) * mm, v(21.73, 13.8) * mm, v(21.97, 13.63) * mm, v(22.4, 13.22) * mm, v(22.68, 12.7) * mm, v(22.6, 12.08) * mm, v(22.38, 11.2) * mm], "startDerivative": vector(27.39, -3.72) * mm, "endDerivative": vector(-3.54, -14.52) * mm});
            skFitSpline(sketch, "E61.trimOffspring", {"points": [v(-52.57, 16.08) * mm, v(-49.1, 13.5) * mm, v(-40.35, 9.2) * mm, v(-31.83, 8.5) * mm, v(-25.06, 10.6) * mm, v(-17, 15.03) * mm, v(-6.97, 16.31) * mm, v(0, 13.63) * mm, v(4.82, 10.36) * mm, v(14.4, 7.56) * mm, v(25.13, 9.66) * mm, v(33.42, 14.1) * mm, v(43, 16.66) * mm, v(50.11, 14.91) * mm, v(51.82, 13.5) * mm], "startDerivative": vector(55.97, -44.86) * mm, "endDerivative": vector(34.72, -36.64) * mm});
            skFitSpline(sketch, "E62", {"points": [v(12.3, 6.37) * mm, v(14.51, 5.17) * mm, v(16.43, 3.2) * mm, v(17, 1.03) * mm, v(15.7, -0.93) * mm, v(13.53, -1.5) * mm, v(11, -0.99) * mm, v(9.6, 0) * mm, v(9.86, 1.4) * mm, v(11.15, 2.32) * mm, v(11.72, 2.12) * mm], "startDerivative": vector(19.8, -9.39) * mm, "endDerivative": vector(8.93, -6.2) * mm});
            skFitSpline(sketch, "E63", {"points": [v(10.43, 6.73) * mm, v(12.86, 5.17) * mm, v(14.57, 4.08) * mm, v(15.8, 2.63) * mm, v(16.22, 0.67) * mm, v(15.24, -0.52) * mm, v(13.58, -0.93) * mm, v(11, -0.47) * mm, v(10, 0) * mm, v(9.83, 0.7) * mm, v(10.38, 1.61) * mm, v(11, 2.09) * mm, v(11.3, 2.13) * mm, v(11.72, 2.12) * mm], "startDerivative": vector(22.23, -15.04) * mm, "endDerivative": vector(10.22, -0.52) * mm});
            skFitSpline(sketch, "E64.trimOffspring", {"points": [v(-53.44, 14.99) * mm, v(-53.15, 14.75) * mm, v(-52.56, 14.28) * mm, v(-51.58, 13.52) * mm, v(-50.63, 12.85) * mm, v(-49.76, 12.26) * mm, v(-48.8, 11.65) * mm, v(-47.47, 10.85) * mm, v(-45.7, 9.88) * mm, v(-43.8, 8.97) * mm, v(-41.82, 8.17) * mm, v(-39.81, 7.55) * mm, v(-37.84, 7.15) * mm, v(-35.9, 6.94) * mm, v(-34.03, 6.9) * mm, v(-32.22, 7.02) * mm, v(-30.48, 7.25) * mm, v(-28.8, 7.62) * mm, v(-27.15, 8.13) * mm, v(-25.8, 8.67) * mm, v(-24.72, 9.18) * mm, v(-23.65, 9.75) * mm, v(-22.35, 10.52) * mm, v(-20.79, 11.48) * mm, v(-19.21, 12.41) * mm, v(-17.6, 13.27) * mm, v(-15.94, 13.97) * mm, v(-14.16, 14.51) * mm, v(-12.32, 14.89) * mm, v(-10.48, 15.08) * mm, v(-8.97, 15.1) * mm, v(-7.81, 15.01) * mm, v(-6.7, 14.87) * mm, v(-5.35, 14.57) * mm, v(-3.85, 14.07) * mm, v(-2.45, 13.44) * mm, v(-1.17, 12.73) * mm, v(-0.02, 11.97) * mm, v(1.09, 11.16) * mm, v(2.27, 10.3) * mm, v(3.61, 9.41) * mm, v(5.2, 8.55) * mm, v(6.98, 7.77) * mm, v(8.94, 7.1) * mm, v(11.02, 6.57) * mm, v(13.2, 6.21) * mm, v(15.42, 6.09) * mm, v(17.63, 6.2) * mm, v(19.8, 6.51) * mm, v(21.9, 7) * mm, v(23.93, 7.64) * mm, v(25.85, 8.42) * mm, v(27.63, 9.29) * mm, v(29.3, 10.2) * mm, v(30.9, 11.13) * mm, v(32.5, 12.04) * mm, v(34.1, 12.89) * mm, v(35.77, 13.66) * mm, v(37.5, 14.31) * mm, v(39.27, 14.83) * mm, v(40.74, 15.11) * mm, v(41.9, 15.23) * mm, v(42.77, 15.27) * mm, v(43.63, 15.25) * mm, v(44.78, 15.15) * mm, v(46.18, 14.9) * mm, v(47.44, 14.54) * mm, v(48.32, 14.22) * mm, v(48.9, 13.97) * mm, v(49.38, 13.72) * mm, v(49.75, 13.5) * mm, v(50.05, 13.27) * mm, v(50.39, 12.98) * mm, v(50.62, 12.74) * mm, v(50.8, 12.55) * mm]});
            skFitSpline(sketch, "E65", {"points": [v(24.2, 7.77) * mm, v(28, 8.15) * mm, v(31.3, 9.25) * mm, v(34.07, 10.27) * mm, v(36.42, 9.4) * mm, v(38.54, 7.93) * mm, v(41.9, 7.5) * mm, v(43.37, 10.42) * mm, v(42.12, 13.42) * mm, v(40.51, 14.22) * mm, v(35.4, 15.76) * mm, v(32.03, 16.27) * mm, v(30.64, 14.8) * mm, v(30.56, 14.8) * mm], "startDerivative": vector(42.5, 2.08) * mm, "endDerivative": vector(-4.74, 2.48) * mm});
            skFitSpline(sketch, "E66", {"points": [v(28.16, 9.58) * mm, v(31.07, 10.34) * mm, v(34, 11.3) * mm, v(36.42, 10.42) * mm, v(39.27, 8.44) * mm, v(41.24, 8.15) * mm, v(42.49, 9.61) * mm, v(41.98, 12.4) * mm, v(38.83, 13.93) * mm, v(34.55, 15.36) * mm, v(32.9, 16) * mm, v(32.06, 15.76) * mm, v(30.64, 14.8) * mm], "startDerivative": vector(31.77, 6.34) * mm, "endDerivative": vector(-22.1, -15.6) * mm});
            skFitSpline(sketch, "E67.trimOffspring", {"points": [v(-53.44, 14.99) * mm, v(-53.15, 14.75) * mm, v(-52.56, 14.28) * mm, v(-51.58, 13.52) * mm, v(-50.63, 12.85) * mm, v(-49.76, 12.26) * mm, v(-48.8, 11.65) * mm, v(-47.47, 10.85) * mm, v(-45.7, 9.88) * mm, v(-43.8, 8.97) * mm, v(-41.82, 8.17) * mm, v(-39.81, 7.55) * mm, v(-37.84, 7.15) * mm, v(-35.9, 6.94) * mm, v(-34.03, 6.9) * mm, v(-32.22, 7.02) * mm, v(-30.48, 7.25) * mm, v(-28.8, 7.62) * mm, v(-27.15, 8.13) * mm, v(-25.8, 8.67) * mm, v(-24.72, 9.18) * mm, v(-23.65, 9.75) * mm, v(-22.35, 10.52) * mm, v(-20.79, 11.48) * mm, v(-19.21, 12.41) * mm, v(-17.6, 13.27) * mm, v(-15.94, 13.97) * mm, v(-14.16, 14.51) * mm, v(-12.32, 14.89) * mm, v(-10.48, 15.08) * mm, v(-8.97, 15.1) * mm, v(-7.81, 15.01) * mm, v(-6.7, 14.87) * mm, v(-5.35, 14.57) * mm, v(-3.85, 14.07) * mm, v(-2.45, 13.44) * mm, v(-1.17, 12.73) * mm, v(-0.02, 11.97) * mm, v(1.09, 11.16) * mm, v(2.27, 10.3) * mm, v(3.61, 9.41) * mm, v(5.2, 8.55) * mm, v(6.98, 7.77) * mm, v(8.94, 7.1) * mm, v(11.02, 6.57) * mm, v(13.2, 6.21) * mm, v(15.42, 6.09) * mm, v(17.63, 6.2) * mm, v(19.8, 6.51) * mm, v(21.9, 7) * mm, v(23.93, 7.64) * mm, v(25.85, 8.42) * mm, v(27.63, 9.29) * mm, v(29.3, 10.2) * mm, v(30.9, 11.13) * mm, v(32.5, 12.04) * mm, v(34.1, 12.89) * mm, v(35.77, 13.66) * mm, v(37.5, 14.31) * mm, v(39.27, 14.83) * mm, v(40.74, 15.11) * mm, v(41.9, 15.23) * mm, v(42.77, 15.27) * mm, v(43.63, 15.25) * mm, v(44.78, 15.15) * mm, v(46.18, 14.9) * mm, v(47.44, 14.54) * mm, v(48.32, 14.22) * mm, v(48.9, 13.97) * mm, v(49.38, 13.72) * mm, v(49.75, 13.5) * mm, v(50.05, 13.27) * mm, v(50.39, 12.98) * mm, v(50.62, 12.74) * mm, v(50.8, 12.55) * mm]});
            skFitSpline(sketch, "E68.trimOffspring", {"points": [v(-53.44, 14.99) * mm, v(-53.15, 14.75) * mm, v(-52.56, 14.28) * mm, v(-51.58, 13.52) * mm, v(-50.63, 12.85) * mm, v(-49.76, 12.26) * mm, v(-48.8, 11.65) * mm, v(-47.47, 10.85) * mm, v(-45.7, 9.88) * mm, v(-43.8, 8.97) * mm, v(-41.82, 8.17) * mm, v(-39.81, 7.55) * mm, v(-37.84, 7.15) * mm, v(-35.9, 6.94) * mm, v(-34.03, 6.9) * mm, v(-32.22, 7.02) * mm, v(-30.48, 7.25) * mm, v(-28.8, 7.62) * mm, v(-27.15, 8.13) * mm, v(-25.8, 8.67) * mm, v(-24.72, 9.18) * mm, v(-23.65, 9.75) * mm, v(-22.35, 10.52) * mm, v(-20.79, 11.48) * mm, v(-19.21, 12.41) * mm, v(-17.6, 13.27) * mm, v(-15.94, 13.97) * mm, v(-14.16, 14.51) * mm, v(-12.32, 14.89) * mm, v(-10.48, 15.08) * mm, v(-8.97, 15.1) * mm, v(-7.81, 15.01) * mm, v(-6.7, 14.87) * mm, v(-5.35, 14.57) * mm, v(-3.85, 14.07) * mm, v(-2.45, 13.44) * mm, v(-1.17, 12.73) * mm, v(-0.02, 11.97) * mm, v(1.09, 11.16) * mm, v(2.27, 10.3) * mm, v(3.61, 9.41) * mm, v(5.2, 8.55) * mm, v(6.98, 7.77) * mm, v(8.94, 7.1) * mm, v(11.02, 6.57) * mm, v(13.2, 6.21) * mm, v(15.42, 6.09) * mm, v(17.63, 6.2) * mm, v(19.8, 6.51) * mm, v(21.9, 7) * mm, v(23.93, 7.64) * mm, v(25.85, 8.42) * mm, v(27.63, 9.29) * mm, v(29.3, 10.2) * mm, v(30.9, 11.13) * mm, v(32.5, 12.04) * mm, v(34.1, 12.89) * mm, v(35.77, 13.66) * mm, v(37.5, 14.31) * mm, v(39.27, 14.83) * mm, v(40.74, 15.11) * mm, v(41.9, 15.23) * mm, v(42.77, 15.27) * mm, v(43.63, 15.25) * mm, v(44.78, 15.15) * mm, v(46.18, 14.9) * mm, v(47.44, 14.54) * mm, v(48.32, 14.22) * mm, v(48.9, 13.97) * mm, v(49.38, 13.72) * mm, v(49.75, 13.5) * mm, v(50.05, 13.27) * mm, v(50.39, 12.98) * mm, v(50.62, 12.74) * mm, v(50.8, 12.55) * mm]});
            skFitSpline(sketch, "E69.trimOffspring", {"points": [v(-52.57, 16.08) * mm, v(-49.1, 13.5) * mm, v(-40.35, 9.2) * mm, v(-31.83, 8.5) * mm, v(-25.06, 10.6) * mm, v(-17, 15.03) * mm, v(-6.97, 16.31) * mm, v(0, 13.63) * mm, v(4.82, 10.36) * mm, v(14.4, 7.56) * mm, v(25.13, 9.66) * mm, v(33.42, 14.1) * mm, v(43, 16.66) * mm, v(50.11, 14.91) * mm, v(51.82, 13.5) * mm], "startDerivative": vector(55.97, -44.86) * mm, "endDerivative": vector(34.72, -36.64) * mm});
            skLineSegment(sketch, "E70", {"start": v(51.82, 19.86) * mm, "end": v(54.22, 22.26) * mm});
            skLineSegment(sketch, "E71", {"start": v(51.82, -19.59) * mm, "end": v(54.22, -22.1) * mm});
            skSolve(sketch);
        }
        {
            var Q0;
            Q0=makeQuery(id+"F1.imprint","IMPRINT",FACE,{"disambiguationData":[TD([[makeQuery(id+"F1.imprint","IMPRINT",EDGE,{"derivedFrom":sQuery(id+"F1.wireOp",EDGE,"E16.0")}),1.0]])]});
            var Q1;
            {var subQ0=sQuery(id+"F1.wireOp",EDGE,"E47");Q1=makeQuery(id+"F1.imprint","IMPRINT",FACE,{"disambiguationData":[TD([[makeQuery(id+"F1.imprint","IMPRINT",EDGE,{"derivedFrom":subQ0}),-1.0]])]});}
            extrude(context, id + "F2", {"entities" : qUnion([Q0, Q1]), "depth" : .75 * mm, "offsetDistance" : 25 * mm});
        }
        {
            var Q0;
            Q0=qSketchRegion(id+"F0",true);
            extrude(context, id + "F3", {"entities" : qUnion([Q0]), "depth" : 1.15 * mm, "offsetDistance" : 25 * mm});
        }
        {
            var Q0;
            {var subQ1=sQuery(id+"F1.wireOp",EDGE,"E14.1");Q0=makeQuery(id+"F1.imprint","IMPRINT",FACE,{"disambiguationData":[TD([[makeQuery(id+"F1.imprint","IMPRINT",EDGE,{"derivedFrom":subQ1}),1.0]])]});}
            var Q1;
            {var subQ5=sQuery(id+"F1.wireOp",EDGE,"E10.left");var subQ6=sQuery(id+"F1.wireOp",EDGE,"E10.top");var subQ7=makeQuery(id+"F1.imprint","INTERSECT",VERTEX,{"derivedFrom":[subQ6,subQ5]});Q1=makeQuery(id+"F1.imprint","IMPRINT",FACE,{"disambiguationData":[TD([[makeQuery(id+"F1.imprint","IMPRINT",EDGE,{"disambiguationData":[TD([[subQ7,-1.0]])],"derivedFrom":subQ6}),1.0]])]});}
            var Q2;
            {var subQ0=sQuery(id+"F1.wireOp",EDGE,"E11.1");Q2=makeQuery(id+"F1.imprint","IMPRINT",FACE,{"disambiguationData":[TD([[makeQuery(id+"F1.imprint","IMPRINT",EDGE,{"derivedFrom":subQ0}),1.0]])]});}
            var Q3;
            {var subQ1=sQuery(id+"F1.wireOp",EDGE,"E14.0");Q3=makeQuery(id+"F1.imprint","IMPRINT",FACE,{"disambiguationData":[TD([[makeQuery(id+"F1.imprint","IMPRINT",EDGE,{"derivedFrom":subQ1}),-1.0]])]});}
            var Q4;
            {var subQ0=sQuery(id+"F1.wireOp",EDGE,"E11.3");Q4=makeQuery(id+"F1.imprint","IMPRINT",FACE,{"disambiguationData":[TD([[makeQuery(id+"F1.imprint","IMPRINT",EDGE,{"derivedFrom":subQ0}),-1.0]])]});}
            var Q5;
            {var subQ0=sQuery(id+"F1.wireOp",EDGE,"E14.2");Q5=makeQuery(id+"F1.imprint","IMPRINT",FACE,{"disambiguationData":[TD([[makeQuery(id+"F1.imprint","IMPRINT",EDGE,{"derivedFrom":subQ0}),1.0]])]});}
            var Q6;
            {var subQ1=sQuery(id+"F1.wireOp",EDGE,"E14.3");Q6=makeQuery(id+"F1.imprint","IMPRINT",FACE,{"disambiguationData":[TD([[makeQuery(id+"F1.imprint","IMPRINT",EDGE,{"derivedFrom":subQ1}),-1.0]])]});}
            var Q7;
            {var subQ6=sQuery(id+"F1.wireOp",EDGE,"E10.right");var subQ8=sQuery(id+"F1.wireOp",EDGE,"E10.bottom");var subQ9=makeQuery(id+"F1.imprint","INTERSECT",VERTEX,{"derivedFrom":[subQ8,subQ6]});Q7=makeQuery(id+"F1.imprint","IMPRINT",FACE,{"disambiguationData":[TD([[makeQuery(id+"F1.imprint","IMPRINT",EDGE,{"disambiguationData":[TD([[subQ9,1.0]])],"derivedFrom":subQ8}),-1.0]])]});}
            extrude(context, id + "F4", {"entities" : qUnion([Q0, Q1, Q2, Q3, Q4, Q5, Q6, Q7]), "depth" : 2 * mm, "offsetDistance" : 25 * mm});
        }
        {
            var Q0;
            Q0=makeQuery(id+"F4.opExtrude","CAP_FACE",FACE,{"disambiguationData":[OSD([sQuery(id+"F1.wireOp",EDGE,"E11.1"),sQuery(id+"F1.wireOp",EDGE,"E11.3"),sQuery(id+"F1.wireOp",EDGE,"E14.0"),sQuery(id+"F1.wireOp",EDGE,"E14.1"),sQuery(id+"F1.wireOp",EDGE,"E14.2"),sQuery(id+"F1.wireOp",EDGE,"E14.3"),sQuery(id+"F1.wireOp",EDGE,"E41"),sQuery(id+"F1.wireOp",EDGE,"E45.trimOffspring"),sQuery(id+"F1.wireOp",EDGE,"E46")])],"isStart":false});
            chamfer(context, id + "F5", {"entities" : qUnion([Q0]), "width" : 1.2 * mm, "tangentPropagation" : true});
        }
    });
